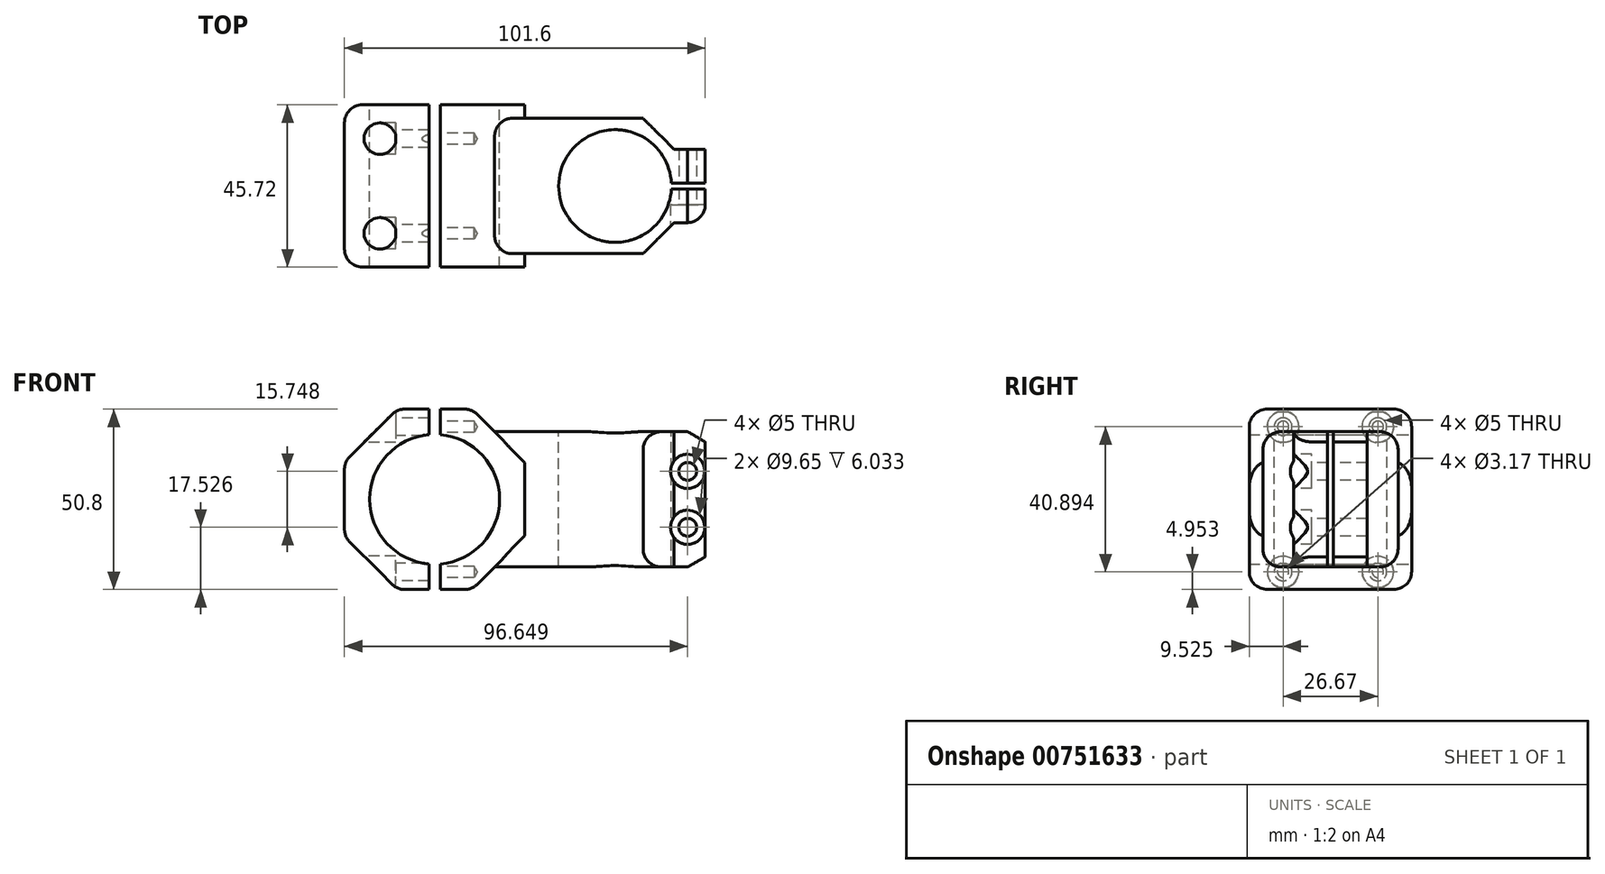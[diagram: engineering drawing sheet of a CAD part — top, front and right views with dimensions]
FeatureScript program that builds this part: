
annotation { "Feature Type Name" : "Feature", "Feature Type Description" : "" }
export const myFeature = defineFeature(function(context is Context, id is Id, definition is map)
    precondition{}
    {
        {
            var Q0;
            Q0=qCreatedBy(makeId("Front.planeOp"),FACE);
            var sketch = newSketch(context, id + "F0", { "sketchPlane" : qUnion([Q0])});
            skLineSegment(sketch, "E0", {"start": v(-50.05, 0) * mm, "end": v(-50.05, 25.4) * mm});
            skLineSegment(sketch, "E1", {"start": v(-50.05, 25.4) * mm, "end": v(51.55, 25.4) * mm});
            skLineSegment(sketch, "E2", {"start": v(51.55, 25.4) * mm, "end": v(51.55, 0) * mm});
            skLineSegment(sketch, "E3.MirrorCS", {"start": v(-50.05, 0) * mm, "end": v(-50.05, -25.4) * mm});
            skLineSegment(sketch, "E4.MirrorCS", {"start": v(-50.05, -25.4) * mm, "end": v(51.55, -25.4) * mm});
            skLineSegment(sketch, "E5.MirrorCS", {"start": v(51.55, -25.4) * mm, "end": v(51.55, 0) * mm});
            skLineSegment(sketch, "E6", {"start": v(-24.65, -25.4) * mm, "end": v(-24.65, 25.4) * mm, "construction": true});
            skCircle(sketch, "E7", {"center": v(-24.65, 0) * mm, "radius": 18.29 * mm});
            skLineSegment(sketch, "E8", {"start": v(-50.05, 10.52) * mm, "end": v(-35.17, 25.4) * mm});
            skLineSegment(sketch, "E9.MirrorCS", {"start": v(0.75, 10.52) * mm, "end": v(-14.13, 25.4) * mm});
            skLineSegment(sketch, "E10.MirrorCS", {"start": v(-50.05, -10.52) * mm, "end": v(-35.17, -25.4) * mm});
            skLineSegment(sketch, "E11.MirrorCS", {"start": v(0.75, -10.52) * mm, "end": v(-14.13, -25.4) * mm});
            skLineSegment(sketch, "E12", {"start": v(51.55, 19.05) * mm, "end": v(-7.78, 19.05) * mm});
            skLineSegment(sketch, "E13.MirrorCS", {"start": v(51.55, -19.05) * mm, "end": v(-7.78, -19.05) * mm});
            skLineSegment(sketch, "E14", {"start": v(46.6, 19.05) * mm, "end": v(46.6, -19.05) * mm, "construction": true});
            skLineSegment(sketch, "E15", {"start": v(46.6, 19.05) * mm, "end": v(51.55, 16.2) * mm});
            skLineSegment(sketch, "E16.MirrorCS", {"start": v(46.6, -19.05) * mm, "end": v(51.55, -16.2) * mm});
            skLineSegment(sketch, "E17", {"start": v(0.75, -10.52) * mm, "end": v(0.75, 10.52) * mm});
            skLineSegment(sketch, "E18", {"start": v(-23.06, 25.4) * mm, "end": v(-23.06, 18.22) * mm});
            skLineSegment(sketch, "E19.MirrorCS", {"start": v(-26.24, 25.4) * mm, "end": v(-26.24, 18.22) * mm});
            skLineSegment(sketch, "E20.MirrorCS", {"start": v(-23.06, -25.4) * mm, "end": v(-23.06, -18.22) * mm});
            skLineSegment(sketch, "E21.MirrorCS", {"start": v(-26.24, -25.4) * mm, "end": v(-26.24, -18.22) * mm});
            skSolve(sketch);
        }
        {
            var Q0;
            {var subQ3=sQuery(id+"F0.wireOp",EDGE,"E8");Q0=makeQuery(id+"F0.imprint","IMPRINT",FACE,{"disambiguationData":[TD([[makeQuery(id+"F0.imprint","IMPRINT",EDGE,{"derivedFrom":subQ3}),-1.0]])]});}
            var Q1;
            {var subQ0=sQuery(id+"F0.wireOp",EDGE,"E17");Q1=makeQuery(id+"F0.imprint","IMPRINT",FACE,{"disambiguationData":[TD([[makeQuery(id+"F0.imprint","IMPRINT",EDGE,{"derivedFrom":subQ0}),1.0]])]});}
            extrude(context, id + "F1", {"entities" : qUnion([Q0, Q1]), "endBound" : BoundingType.SYMMETRIC, "depth" : 45.72 * mm, "offsetDistance" : 25.4 * mm});
        }
        {
            var Q0;
            {var subQ11=sQuery(id+"F0.wireOp",EDGE,"E15");Q0=makeQuery(id+"F0.imprint","IMPRINT",FACE,{"disambiguationData":[TD([[makeQuery(id+"F0.imprint","IMPRINT",EDGE,{"derivedFrom":subQ11}),-1.0]])]});}
            extrude(context, id + "F2", {"entities" : qUnion([Q0]), "operationType" : NewBodyOperationType.ADD, "endBound" : BoundingType.SYMMETRIC, "depth" : 38.1 * mm, "offsetDistance" : 25.4 * mm});
        }
        {
            var Q0;
            Q0=qCreatedBy(makeId("Top.planeOp"),FACE);
            var sketch = newSketch(context, id + "F3", { "sketchPlane" : qUnion([Q0])});
            skCircle(sketch, "E22", {"center": v(26.15, 0) * mm, "radius": 15.88 * mm});
            skLineSegment(sketch, "E23", {"start": v(42, -0.8) * mm, "end": v(51.55, -0.8) * mm});
            skLineSegment(sketch, "E24.MirrorCS", {"start": v(42, 0.8) * mm, "end": v(51.55, 0.8) * mm});
            skLineSegment(sketch, "E25", {"start": v(51.55, 0.8) * mm, "end": v(51.55, 10.32) * mm});
            skLineSegment(sketch, "E26", {"start": v(51.55, 10.32) * mm, "end": v(42.77, 10.32) * mm});
            skLineSegment(sketch, "E27", {"start": v(42.77, 10.32) * mm, "end": v(34.04, 19.05) * mm});
            skLineSegment(sketch, "E28", {"start": v(34.04, 19.05) * mm, "end": v(51.55, 19.05) * mm});
            skLineSegment(sketch, "E29", {"start": v(51.55, 19.05) * mm, "end": v(51.55, 10.32) * mm});
            skLineSegment(sketch, "E30.MirrorCS", {"start": v(51.55, -0.8) * mm, "end": v(51.55, -10.32) * mm});
            skLineSegment(sketch, "E31.MirrorCS", {"start": v(51.55, -10.32) * mm, "end": v(42.77, -10.32) * mm});
            skLineSegment(sketch, "E32.MirrorCS", {"start": v(42.77, -10.32) * mm, "end": v(34.04, -19.05) * mm});
            skLineSegment(sketch, "E33.MirrorCS", {"start": v(34.04, -19.05) * mm, "end": v(51.55, -19.05) * mm});
            skLineSegment(sketch, "E34.MirrorCS", {"start": v(51.55, -19.05) * mm, "end": v(51.55, -10.32) * mm});
            skLineSegment(sketch, "E35", {"start": v(51.55, -0.8) * mm, "end": v(51.55, 0.8) * mm});
            skSolve(sketch);
        }
        {
            var Q0;
            {var subQ0=sQuery(id+"F3.wireOp",EDGE,"E22");var subQ1=makeQuery(id+"F3.imprint","INTERSECT",VERTEX,{"derivedFrom":[subQ0,sQuery(id+"F3.wireOp",EDGE,"E23")]});Q0=makeQuery(id+"F3.imprint","IMPRINT",FACE,{"disambiguationData":[TD([[makeQuery(id+"F3.imprint","IMPRINT",EDGE,{"disambiguationData":[TD([[subQ1,1.0]])],"derivedFrom":subQ0}),1.0]])]});}
            var Q1;
            {var subQ0=sQuery(id+"F3.wireOp",EDGE,"E23");Q1=makeQuery(id+"F3.imprint","IMPRINT",FACE,{"disambiguationData":[TD([[makeQuery(id+"F3.imprint","IMPRINT",EDGE,{"derivedFrom":subQ0}),1.0]])]});}
            var Q2;
            Q2=makeQuery(id+"F3.imprint","IMPRINT",FACE,{"disambiguationData":[TD([[makeQuery(id+"F3.imprint","IMPRINT",EDGE,{"derivedFrom":sQuery(id+"F3.wireOp",EDGE,"E26")}),-1.0]])]});
            var Q3;
            Q3=makeQuery(id+"F3.imprint","IMPRINT",FACE,{"disambiguationData":[TD([[makeQuery(id+"F3.imprint","IMPRINT",EDGE,{"derivedFrom":sQuery(id+"F3.wireOp",EDGE,"E31.MirrorCS")}),1.0]])]});
            extrude(context, id + "F4", {"entities" : qUnion([Q0, Q1, Q2, Q3]), "operationType" : NewBodyOperationType.REMOVE, "endBound" : BoundingType.SYMMETRIC, "oppositeDirection" : true, "depth" : 38.1 * mm, "offsetDistance" : 25.4 * mm});
        }
        {
            var Q0;
            Q0=makeQuery(id+"F2.opExtrude","CAP_FACE",FACE,{"disambiguationData":[OSD([sQuery(id+"F0.wireOp",EDGE,"E2"),sQuery(id+"F0.wireOp",EDGE,"E5.MirrorCS"),sQuery(id+"F0.wireOp",EDGE,"E9.MirrorCS"),sQuery(id+"F0.wireOp",EDGE,"E11.MirrorCS"),sQuery(id+"F0.wireOp",EDGE,"E12"),sQuery(id+"F0.wireOp",EDGE,"E13.MirrorCS"),sQuery(id+"F0.wireOp",EDGE,"E15"),sQuery(id+"F0.wireOp",EDGE,"E16.MirrorCS"),sQuery(id+"F0.wireOp",EDGE,"E17")])],"isStart":false});
            var sketch = newSketch(context, id + "F5", { "sketchPlane" : qUnion([Q0])});
            skCircle(sketch, "E36", {"center": v(46.6, 7.87) * mm, "radius": 4.83 * mm});
            skCircle(sketch, "E37.MirrorC", {"center": v(46.6, -7.87) * mm, "radius": 4.83 * mm});
            skSolve(sketch);
        }
        {
            var Q0;
            Q0=sQuery(id+"F5.wireOp",VERTEX,"E36.center");
            var Q1;
            Q1=sQuery(id+"F5.wireOp",VERTEX,"E37.MirrorC.center");
            var Q2;
            Q2=makeQuery(id+"F1.opExtrude","SWEPT_BODY",BODY,{"disambiguationData":[OSD([sQuery(id+"F0.wireOp",EDGE,"E1"),sQuery(id+"F0.wireOp",EDGE,"E4.MirrorCS"),sQuery(id+"F0.wireOp",EDGE,"E7"),sQuery(id+"F0.wireOp",EDGE,"E9.MirrorCS"),sQuery(id+"F0.wireOp",EDGE,"E11.MirrorCS"),sQuery(id+"F0.wireOp",EDGE,"E17"),sQuery(id+"F0.wireOp",EDGE,"E18"),sQuery(id+"F0.wireOp",EDGE,"E20.MirrorCS")])]});
            hole(context, id + "F6", {"style" : HoleStyle.C_BORE, "endStyle" : HoleEndStyle.THROUGH, "holeDiameter" : 5 * mm, "cBoreDiameter" : 9.65 * mm, "cBoreDepth" : 5.03 * mm, "majorDiameter" : 6.35 * mm, "isTappedThrough" : true, "tappedDepth" : 12.7 * mm, "tapClearance" : 3, "locations" : qUnion([Q0, Q1]), "scope" : qUnion([Q2])});
        }
        {
            var Q0;
            Q0=makeQuery(id+"F1.opExtrude","SWEPT_FACE",FACE,{"disambiguationData":[OSD([sQuery(id+"F0.wireOp",EDGE,"E0"),sQuery(id+"F0.wireOp",EDGE,"E3.MirrorCS")])]});
            var sketch = newSketch(context, id + "F7", { "sketchPlane" : qUnion([Q0])});
            skLineSegment(sketch, "E38", {"start": v(-33, 20.45) * mm, "end": v(32.38, 20.45) * mm, "construction": true});
            skCircle(sketch, "E39", {"center": v(-13.34, 20.45) * mm, "radius": 3.34 * mm});
            skCircle(sketch, "E40.MirrorC", {"center": v(13.34, 20.45) * mm, "radius": 3.34 * mm});
            skCircle(sketch, "E41.MirrorC", {"center": v(-13.34, -20.45) * mm, "radius": 3.34 * mm});
            skCircle(sketch, "E42.MirrorC", {"center": v(13.34, -20.45) * mm, "radius": 3.34 * mm});
            skSolve(sketch);
        }
        {
            var Q0;
            Q0=sQuery(id+"F7.wireOp",VERTEX,"E39.center");
            var Q1;
            Q1=sQuery(id+"F7.wireOp",VERTEX,"E40.MirrorC.center");
            var Q2;
            Q2=sQuery(id+"F7.wireOp",VERTEX,"E41.MirrorC.center");
            var Q3;
            Q3=sQuery(id+"F7.wireOp",VERTEX,"E42.MirrorC.center");
            var Q4;
            Q4=makeQuery(id+"F1.opExtrude","SWEPT_BODY",BODY,{"disambiguationData":[OSD([sQuery(id+"F0.wireOp",EDGE,"E1"),sQuery(id+"F0.wireOp",EDGE,"E4.MirrorCS"),sQuery(id+"F0.wireOp",EDGE,"E7"),sQuery(id+"F0.wireOp",EDGE,"E9.MirrorCS"),sQuery(id+"F0.wireOp",EDGE,"E11.MirrorCS"),sQuery(id+"F0.wireOp",EDGE,"E17"),sQuery(id+"F0.wireOp",EDGE,"E18"),sQuery(id+"F0.wireOp",EDGE,"E20.MirrorCS")])]});
            var Q5;
            Q5=makeQuery(id+"F1.opExtrude","SWEPT_BODY",BODY,{"disambiguationData":[OSD([sQuery(id+"F0.wireOp",EDGE,"E0"),sQuery(id+"F0.wireOp",EDGE,"E1"),sQuery(id+"F0.wireOp",EDGE,"E3.MirrorCS"),sQuery(id+"F0.wireOp",EDGE,"E4.MirrorCS"),sQuery(id+"F0.wireOp",EDGE,"E7"),sQuery(id+"F0.wireOp",EDGE,"E8"),sQuery(id+"F0.wireOp",EDGE,"E10.MirrorCS"),sQuery(id+"F0.wireOp",EDGE,"E19.MirrorCS"),sQuery(id+"F0.wireOp",EDGE,"E21.MirrorCS")])]});
            hole(context, id + "F8", {"style" : HoleStyle.C_BORE, "endStyle" : HoleEndStyle.BLIND_IN_LAST, "holeDiameter" : 5 * mm, "cBoreDiameter" : 8.9 * mm, "cBoreDepth" : 0.03 * mm, "tapDrillDiameter" : 3.17 * mm, "majorDiameter" : 6.35 * mm, "holeDepth" : 9.52 * mm, "isTappedThrough" : true, "tappedDepth" : 12.7 * mm, "tapClearance" : 3, "locations" : qUnion([Q0, Q1, Q2, Q3]), "scope" : qUnion([Q4, Q5])});
        }
        {
            var Q0;
            Q0=makeQuery(id+"F1.opExtrude","SWEPT_EDGE",EDGE,{"disambiguationData":[OSD([sQuery(id+"F0.wireOp",EDGE,"E1"),sQuery(id+"F0.wireOp",EDGE,"E9.MirrorCS")])]});
            var Q1;
            Q1=makeQuery(id+"F1.opExtrude","SWEPT_EDGE",EDGE,{"disambiguationData":[OSD([sQuery(id+"F0.wireOp",EDGE,"E1"),sQuery(id+"F0.wireOp",EDGE,"E8")])]});
            var Q2;
            Q2=makeQuery(id+"F1.opExtrude","SWEPT_EDGE",EDGE,{"disambiguationData":[OSD([sQuery(id+"F0.wireOp",EDGE,"E0"),sQuery(id+"F0.wireOp",EDGE,"E8")])]});
            var Q3;
            Q3=makeQuery(id+"F1.opExtrude","SWEPT_EDGE",EDGE,{"disambiguationData":[OSD([sQuery(id+"F0.wireOp",EDGE,"E3.MirrorCS"),sQuery(id+"F0.wireOp",EDGE,"E10.MirrorCS")])]});
            var Q4;
            Q4=makeQuery(id+"F1.opExtrude","SWEPT_EDGE",EDGE,{"disambiguationData":[OSD([sQuery(id+"F0.wireOp",EDGE,"E4.MirrorCS"),sQuery(id+"F0.wireOp",EDGE,"E10.MirrorCS")])]});
            var Q5;
            Q5=makeQuery(id+"F1.opExtrude","SWEPT_EDGE",EDGE,{"disambiguationData":[OSD([sQuery(id+"F0.wireOp",EDGE,"E4.MirrorCS"),sQuery(id+"F0.wireOp",EDGE,"E11.MirrorCS")])]});
            var Q6;
            Q6=makeQuery(id+"F4.boolean.opBoolean","COPY",EDGE,{"derivedFrom":makeQuery(id+"F4.opExtrude","SWEPT_EDGE",EDGE,{"disambiguationData":[OSD([sQuery(id+"F3.wireOp",EDGE,"E27"),sQuery(id+"F3.wireOp",EDGE,"E28")])]})});
            var Q7;
            Q7=makeQuery(id+"F4.boolean.opBoolean","COPY",EDGE,{"derivedFrom":makeQuery(id+"F4.opExtrude","SWEPT_EDGE",EDGE,{"disambiguationData":[OSD([sQuery(id+"F3.wireOp",EDGE,"E26"),sQuery(id+"F3.wireOp",EDGE,"E29")])]})});
            var Q8;
            Q8=makeQuery(id+"F4.boolean.opBoolean","COPY",EDGE,{"derivedFrom":makeQuery(id+"F4.opExtrude","SWEPT_EDGE",EDGE,{"disambiguationData":[OSD([sQuery(id+"F3.wireOp",EDGE,"E31.MirrorCS"),sQuery(id+"F3.wireOp",EDGE,"E34.MirrorCS")])]})});
            var Q9;
            Q9=makeQuery(id+"F4.boolean.opBoolean","COPY",EDGE,{"derivedFrom":makeQuery(id+"F4.opExtrude","SWEPT_EDGE",EDGE,{"disambiguationData":[OSD([sQuery(id+"F3.wireOp",EDGE,"E32.MirrorCS"),sQuery(id+"F3.wireOp",EDGE,"E33.MirrorCS")])]})});
            var Q10;
            Q10=makeQuery(id+"F2.opExtrude","CAP_EDGE",EDGE,{"disambiguationData":[OSD([sQuery(id+"F0.wireOp",EDGE,"E12")])],"isStart":false});
            var Q11;
            Q11=makeQuery(id+"F2.opExtrude","CAP_EDGE",EDGE,{"disambiguationData":[OSD([sQuery(id+"F0.wireOp",EDGE,"E12")])],"isStart":true});
            var Q12;
            Q12=makeQuery(id+"F2.opExtrude","CAP_EDGE",EDGE,{"disambiguationData":[OSD([sQuery(id+"F0.wireOp",EDGE,"E13.MirrorCS")])],"isStart":true});
            var Q13;
            Q13=makeQuery(id+"F2.opExtrude","CAP_EDGE",EDGE,{"disambiguationData":[OSD([sQuery(id+"F0.wireOp",EDGE,"E13.MirrorCS")])],"isStart":false});
            fillet(context, id + "F9", {"entities" : qUnion([Q0, Q1, Q2, Q3, Q4, Q5, Q6, Q7, Q8, Q9, Q10, Q11, Q12, Q13]), "radius" : 5.08 * mm, "tangentPropagation" : true, "allowEdgeOverflow" : false});
        }
        {
            var Q0;
            Q0=makeQuery(id+"F1.opExtrude","CAP_EDGE",EDGE,{"disambiguationData":[OSD([sQuery(id+"F0.wireOp",EDGE,"E10.MirrorCS")])],"isStart":true});
            var Q1;
            Q1=makeQuery(id+"F1.opExtrude","CAP_EDGE",EDGE,{"disambiguationData":[OSD([sQuery(id+"F0.wireOp",EDGE,"E10.MirrorCS")])],"isStart":false});
            var Q2;
            Q2=makeQuery(id+"F1.opExtrude","CAP_EDGE",EDGE,{"disambiguationData":[OSD([sQuery(id+"F0.wireOp",EDGE,"E11.MirrorCS")])],"isStart":false});
            var Q3;
            Q3=makeQuery(id+"F1.opExtrude","CAP_EDGE",EDGE,{"disambiguationData":[OSD([sQuery(id+"F0.wireOp",EDGE,"E9.MirrorCS")])],"isStart":false});
            var Q4;
            Q4=makeQuery(id+"F1.opExtrude","CAP_EDGE",EDGE,{"disambiguationData":[OSD([sQuery(id+"F0.wireOp",EDGE,"E9.MirrorCS")])],"isStart":true});
            var Q5;
            Q5=makeQuery(id+"F1.opExtrude","CAP_EDGE",EDGE,{"disambiguationData":[OSD([sQuery(id+"F0.wireOp",EDGE,"E11.MirrorCS")])],"isStart":true});
            fillet(context, id + "F10", {"entities" : qUnion([Q0, Q1, Q2, Q3, Q4, Q5]), "radius" : 5.08 * mm, "tangentPropagation" : true, "allowEdgeOverflow" : false});
        }
    });
